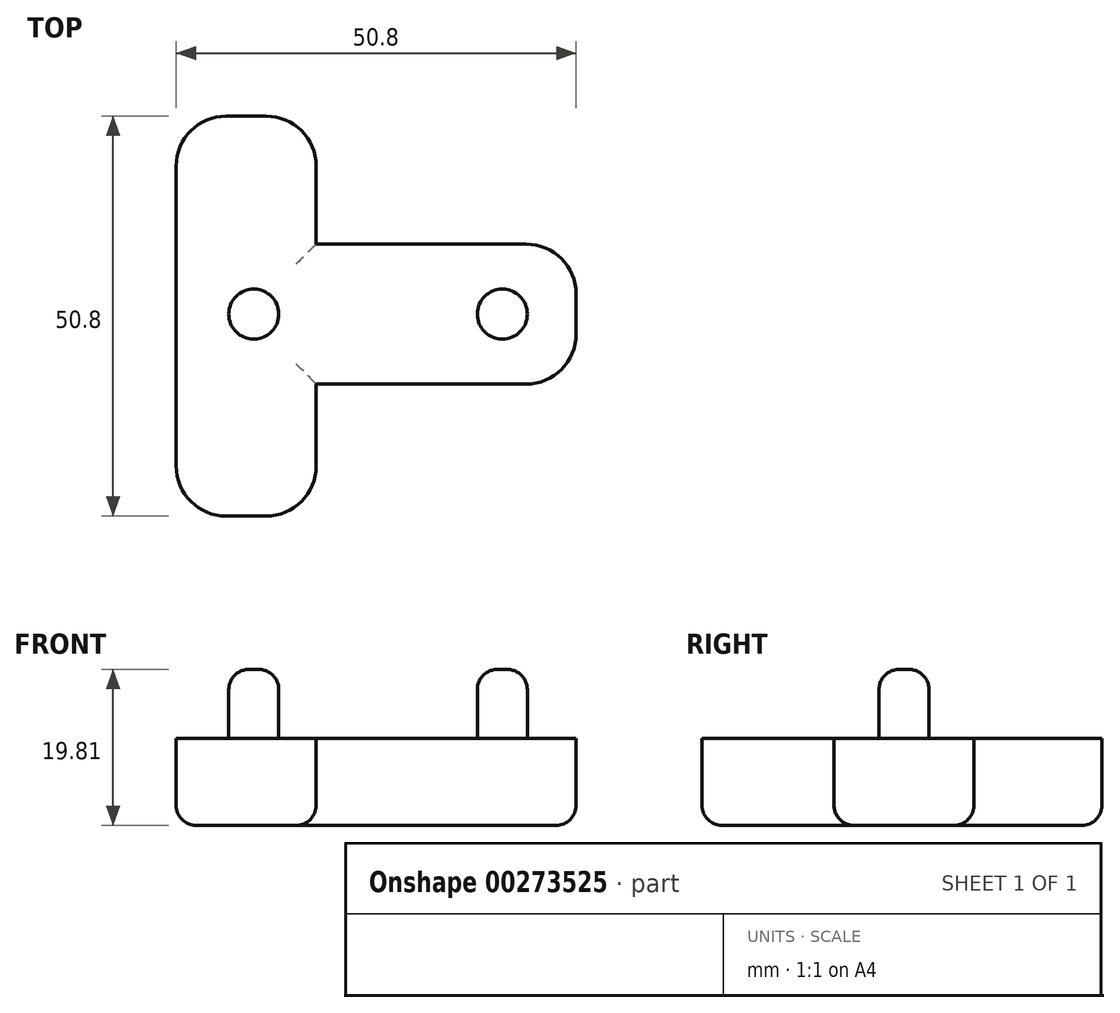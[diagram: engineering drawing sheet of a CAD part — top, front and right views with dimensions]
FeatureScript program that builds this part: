
annotation { "Feature Type Name" : "Feature", "Feature Type Description" : "" }
export const myFeature = defineFeature(function(context is Context, id is Id, definition is map)
    precondition{}
    {
        {
            var Q0;
            Q0=qCreatedBy(makeId("Top.planeOp"),FACE);
            var sketch = newSketch(context, id + "F0", { "sketchPlane" : qUnion([Q0])});
            skLineSegment(sketch, "E0.bottom", {"start": v(19.05, -8.9) * mm, "end": v(-25.4, -8.9) * mm});
            skLineSegment(sketch, "E0.top", {"start": v(19.05, 8.9) * mm, "end": v(-25.4, 8.9) * mm});
            skLineSegment(sketch, "E0.left", {"start": v(25.4, -2.54) * mm, "end": v(25.4, 2.54) * mm});
            skLineSegment(sketch, "E0.right", {"start": v(-25.4, -8.9) * mm, "end": v(-25.4, 8.89) * mm});
            skPoint(sketch, "E0.middle", {"position": v(0, 0) * mm});
            skLineSegment(sketch, "E1.bottom", {"start": v(-19.05, 25.15) * mm, "end": v(-13.97, 25.15) * mm});
            skLineSegment(sketch, "E1.top", {"start": v(-19.05, -25.65) * mm, "end": v(-13.97, -25.65) * mm});
            skLineSegment(sketch, "E1.left", {"start": v(-25.4, 18.8) * mm, "end": v(-25.4, -19.3) * mm});
            skLineSegment(sketch, "E1.right", {"start": v(-7.62, 18.8) * mm, "end": v(-7.62, -19.3) * mm});
            skPoint(sketch, "E2.visualSharp", {"position": v(-25.4, 25.15) * mm});
            skArc(sketch, "E2.filletArc", {"start": v(-19.05, 25.15) * mm, "mid": v(-23.54, 23.29) * mm, "end": v(-25.4, 18.8) * mm});
            skPoint(sketch, "E3.visualSharp", {"position": v(-25.4, -25.65) * mm});
            skArc(sketch, "E3.filletArc", {"start": v(-25.4, -19.3) * mm, "mid": v(-23.54, -23.8) * mm, "end": v(-19.05, -25.65) * mm});
            skPoint(sketch, "E4.visualSharp", {"position": v(-7.62, 25.15) * mm});
            skArc(sketch, "E4.filletArc", {"start": v(-7.62, 18.8) * mm, "mid": v(-9.48, 23.29) * mm, "end": v(-13.97, 25.15) * mm});
            skPoint(sketch, "E5.visualSharp", {"position": v(25.4, 8.9) * mm});
            skArc(sketch, "E5.filletArc", {"start": v(25.4, 2.54) * mm, "mid": v(23.54, 7.03) * mm, "end": v(19.05, 8.9) * mm});
            skPoint(sketch, "E6.visualSharp", {"position": v(25.4, -8.9) * mm});
            skArc(sketch, "E6.filletArc", {"start": v(19.05, -8.9) * mm, "mid": v(23.54, -7.03) * mm, "end": v(25.4, -2.54) * mm});
            skPoint(sketch, "E7.visualSharp", {"position": v(-7.62, -25.65) * mm});
            skArc(sketch, "E7.filletArc", {"start": v(-13.97, -25.65) * mm, "mid": v(-9.48, -23.8) * mm, "end": v(-7.62, -19.3) * mm});
            skSolve(sketch);
        }
        {
            var Q0;
            {var subQ0=sQuery(id+"F0.wireOp",EDGE,"E1.left");var subQ1=sQuery(id+"F0.wireOp",EDGE,"E0.bottom");var subQ2=makeQuery(id+"F0.imprint","INTERSECT",VERTEX,{"derivedFrom":[subQ1,subQ0]});Q0=makeQuery(id+"F0.imprint","IMPRINT",FACE,{"disambiguationData":[TD([[makeQuery(id+"F0.imprint","IMPRINT",EDGE,{"disambiguationData":[TD([[subQ2,1.0]])],"derivedFrom":subQ1}),-1.0]])]});}
            var Q1;
            Q1=makeQuery(id+"F0.imprint","IMPRINT",FACE,{"disambiguationData":[TD([[makeQuery(id+"F0.imprint","IMPRINT",EDGE,{"derivedFrom":sQuery(id+"F0.wireOp",EDGE,"E1.top")}),1.0]])]});
            var Q2;
            Q2=makeQuery(id+"F0.imprint","IMPRINT",FACE,{"disambiguationData":[TD([[makeQuery(id+"F0.imprint","IMPRINT",EDGE,{"derivedFrom":sQuery(id+"F0.wireOp",EDGE,"E1.bottom")}),-1.0]])]});
            var Q3;
            Q3=makeQuery(id+"F0.imprint","IMPRINT",FACE,{"disambiguationData":[TD([[makeQuery(id+"F0.imprint","IMPRINT",EDGE,{"derivedFrom":sQuery(id+"F0.wireOp",EDGE,"E0.left")}),1.0]])]});
            extrude(context, id + "F1", {"entities" : qUnion([Q0, Q1, Q2, Q3]), "depth" : 11.05 * mm});
        }
        {
            var Q0;
            {var subQ0=sQuery(id+"F0.wireOp",EDGE,"E1.right");Q0=makeQuery(id+"F1.opExtrude","CAP_EDGE",EDGE,{"disambiguationData":[OSD([subQ0]),TDD([makeQuery(id+"F0.imprint","IMPRINT",EDGE,{"disambiguationData":[TD([[makeQuery(id+"F0.imprint","INTERSECT",VERTEX,{"derivedFrom":[subQ0,sQuery(id+"F0.wireOp",EDGE,"E7.filletArc")]}),1.0]])],"derivedFrom":subQ0})])],"isStart":true});}
            var Q1;
            Q1=makeQuery(id+"F1.opExtrude","CAP_EDGE",EDGE,{"disambiguationData":[OSD([sQuery(id+"F0.wireOp",EDGE,"E0.bottom")])],"isStart":true});
            var Q2;
            Q2=makeQuery(id+"F1.opExtrude","CAP_EDGE",EDGE,{"disambiguationData":[OSD([sQuery(id+"F0.wireOp",EDGE,"E6.filletArc")])],"isStart":true});
            fillet(context, id + "F2", {"entities" : qUnion([Q0, Q1, Q2]), "radius" : 2.54 * mm, "tangentPropagation" : true, "allowEdgeOverflow" : false});
        }
        {
            var Q0;
            Q0=makeQuery(id+"F1.opExtrude","CAP_FACE",FACE,{"disambiguationData":[OSD([sQuery(id+"F0.wireOp",EDGE,"E0.bottom"),sQuery(id+"F0.wireOp",EDGE,"E0.top"),sQuery(id+"F0.wireOp",EDGE,"E0.left"),sQuery(id+"F0.wireOp",EDGE,"E1.bottom"),sQuery(id+"F0.wireOp",EDGE,"E1.top"),sQuery(id+"F0.wireOp",EDGE,"E1.left"),sQuery(id+"F0.wireOp",EDGE,"E1.right"),sQuery(id+"F0.wireOp",EDGE,"E2.filletArc"),sQuery(id+"F0.wireOp",EDGE,"E3.filletArc"),sQuery(id+"F0.wireOp",EDGE,"E4.filletArc"),sQuery(id+"F0.wireOp",EDGE,"E5.filletArc"),sQuery(id+"F0.wireOp",EDGE,"E6.filletArc"),sQuery(id+"F0.wireOp",EDGE,"E7.filletArc")])],"isStart":false});
            var sketch = newSketch(context, id + "F3", { "sketchPlane" : qUnion([Q0])});
            skCircle(sketch, "E8", {"center": v(16.02, 0) * mm, "radius": 3.18 * mm});
            skCircle(sketch, "E9", {"center": v(-15.54, 0) * mm, "radius": 3.18 * mm});
            skSolve(sketch);
        }
        {
            var Q0;
            Q0=makeQuery(id+"F3.imprint","IMPRINT",FACE,{"disambiguationData":[TD([[makeQuery(id+"F3.imprint","IMPRINT",EDGE,{"derivedFrom":sQuery(id+"F3.wireOp",EDGE,"E8")}),1.0]])]});
            var Q1;
            Q1=makeQuery(id+"F3.imprint","IMPRINT",FACE,{"disambiguationData":[TD([[makeQuery(id+"F3.imprint","IMPRINT",EDGE,{"derivedFrom":sQuery(id+"F3.wireOp",EDGE,"E9")}),1.0]])]});
            extrude(context, id + "F4", {"entities" : qUnion([Q0, Q1]), "operationType" : NewBodyOperationType.ADD, "depth" : 8.76 * mm});
        }
        {
            var Q0;
            Q0=makeQuery(id+"F4.opExtrude","CAP_EDGE",EDGE,{"disambiguationData":[OSD([sQuery(id+"F3.wireOp",EDGE,"E9")])],"isStart":false});
            var Q1;
            Q1=makeQuery(id+"F4.opExtrude","CAP_EDGE",EDGE,{"disambiguationData":[OSD([sQuery(id+"F3.wireOp",EDGE,"E8")])],"isStart":false});
            fillet(context, id + "F5", {"entities" : qUnion([Q0, Q1]), "radius" : 2.54 * mm, "tangentPropagation" : true, "allowEdgeOverflow" : false});
        }
    });
